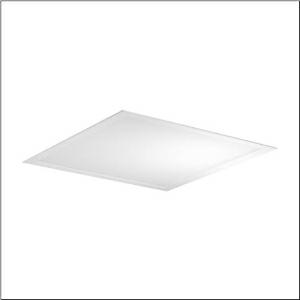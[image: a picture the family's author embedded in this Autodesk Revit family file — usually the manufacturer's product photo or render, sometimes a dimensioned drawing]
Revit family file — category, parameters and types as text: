
# Revit family: apollon_r__31_square_51mp11w72442_ea88
name_source: partatom
category: Lighting Fixtures
units: mm (PartAtom-declared; Revit-internal decimal feet)

## family parameters
Cut with Voids When Loaded = No
Host = Face
Light Source = No
Part Type = Normal
Room Calculation Point = No
Round Connector Dimension = Use Diameter
Shared = No

## types (1)
- Apollon® 31 square (1 x LED, 4000 lm, 27.5 W, 4000K)
    Apparent Load = 28 VA
    CIE Flux Codes = 61 87 97 100 100
    Color Rendering = 80
    Color Temperature = 4000K
    Default Elevation = 1800 mm
    Description = Apollon® 31 square, office luminaire, primary optical cover: micro prismatic cover, of PMMA, CAT 2 (L<= 3000cd/m²), light emission: direct distribution, primary light characteristic: symmetric, installation type: lay-in mounting, LED, rated luminous flux: 4.000lm, luminous efficacy: 145lm/W, light colour: 840, colour temperature: 4000K, control gear: ON/OFF, with terminal, 3-pole, mains connection: 220..240V, AC, 50/60Hz, rated input power: 28W, housing, of aluminium, traffic white (RAL 9016), module: M625, length: 620mm, width: 620mm, height: 62mm, recess depth: 180mm, housing upper side, of sheet steel, coated, protection rating (complete): IP20, protection rating (on room side): IP40, insulation class (complete): insulation class II (safety insulation), certification: CE, ENEC, impact resistance: IK03, permissible operating ambient temperature: -20..+40°C, permissible storage temperature: -20..+60°C, packaging unit: 1 piece
    Height = 0 mm  [stored 0 ft]
    Lamp = 1 x LED
    Lamp Light Flux = 4000 lm
    Lamp Power = 27.5 W
    Lamp count = 1
    Length = 620 mm
    Luminous efficacy = 145 lm/W
    Manufacturer = Siteco
    ModVariant = No
    Model = 51MP11W72442
    Mounting Place = Ceiling
    Mounting Type = Recessed
    Number of Poles = 1
    OnlyDefault = Yes
    Power Factor = 1
    Product Name = Apollon® 31 square
    Product group = office luminaire | ceiling recessed
    ProductGroupID = 401
    Protection Class = Protection class II
    Protection Degree = IP 20
    RLX_Detail_Level = 1
    RLX_Emergency_Light_Flux = 0 lm
    RLX_Emergency_Type = 0
    RLX_Emergency_Type_DB = No
    RlxData = <blob elided: 12973 chars, md5=5928af6b>
    Socket = socket
    Standby Power = 0 W
    System Light Flux = 4000 lm
    System Power = 28 W
    Type Comments = Product without accessories
    Type Image = l_1291039.jpg
    URL = http://relux.com
    VarID = ---
    Voltage = 0 V
    Weight = 0.00 kg
    Width = 620 mm

note: [stored X ft] marks values corroborated as IEEE doubles in the binary element streams (Revit-internal decimal feet)

## geometry (parser evidence)
native form markers: Sweep x9
no freeform markers — native parametric forms only
